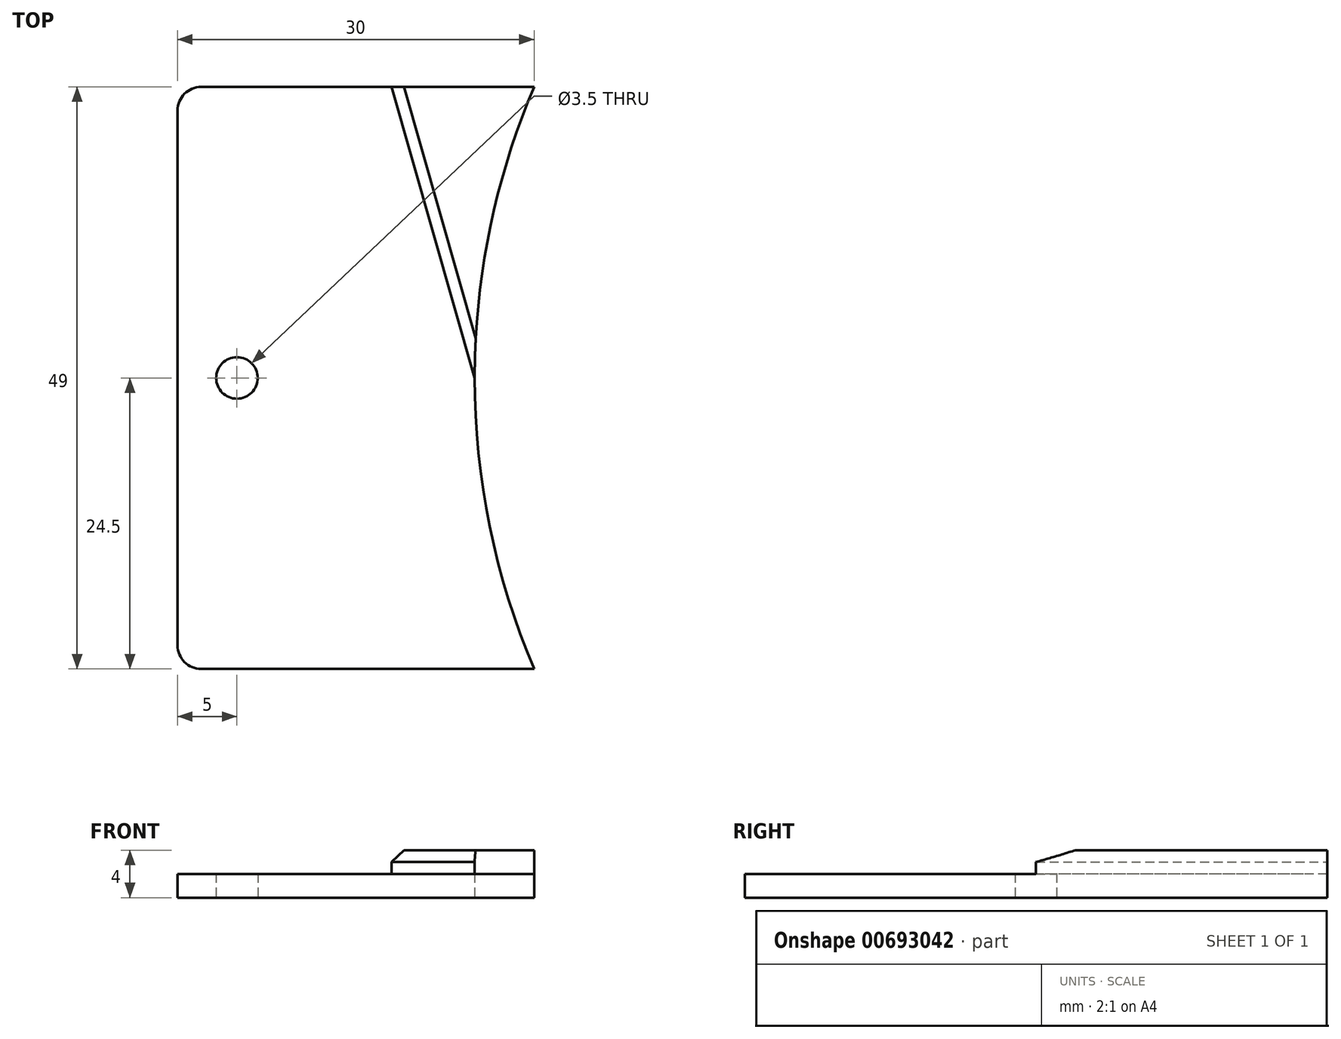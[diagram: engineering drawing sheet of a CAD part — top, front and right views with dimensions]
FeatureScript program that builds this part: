
annotation { "Feature Type Name" : "Feature", "Feature Type Description" : "" }
export const myFeature = defineFeature(function(context is Context, id is Id, definition is map)
    precondition{}
    {
        {
            var Q0;
            Q0=qCreatedBy(makeId("Top.planeOp"),FACE);
            var sketch = newSketch(context, id + "F0", { "sketchPlane" : qUnion([Q0])});
            skLineSegment(sketch, "E0", {"start": v(0, 0) * mm, "end": v(-100, 0) * mm, "construction": true});
            skLineSegment(sketch, "E1.bottom", {"start": v(-87.5, 24.5) * mm, "end": v(-27.5, 24.5) * mm});
            skLineSegment(sketch, "E1.top", {"start": v(-87.5, -24.5) * mm, "end": v(-27.5, -24.5) * mm});
            skLineSegment(sketch, "E1.left", {"start": v(-87.5, 24.5) * mm, "end": v(-87.5, -24.5) * mm});
            skLineSegment(sketch, "E1.right", {"start": v(-27.5, 24.5) * mm, "end": v(-27.5, -24.5) * mm});
            skPoint(sketch, "E1.middle", {"position": v(-57.5, 0) * mm});
            skCircle(sketch, "E2", {"center": v(0, 0) * mm, "radius": 62.5 * mm});
            skPoint(sketch, "E3", {"position": v(-69.5, 24.5) * mm});
            skPoint(sketch, "E4", {"position": v(-62.5, 0) * mm});
            skLineSegment(sketch, "E5", {"start": v(-69.5, 24.5) * mm, "end": v(-62.5, 0) * mm});
            skCircle(sketch, "E6", {"center": v(-82.5, 0) * mm, "radius": 1.75 * mm});
            skSolve(sketch);
        }
        {
            var Q0;
            {var subQ0=sQuery(id+"F0.wireOp",EDGE,"E5");Q0=makeQuery(id+"F0.imprint","IMPRINT",FACE,{"disambiguationData":[TD([[makeQuery(id+"F0.imprint","IMPRINT",EDGE,{"derivedFrom":subQ0}),1.0]])]});}
            extrude(context, id + "F1", {"entities" : qUnion([Q0]), "depth" : 4 * mm, "offsetDistance" : 25 * mm});
        }
        {
            var Q0;
            {var subQ4=sQuery(id+"F0.wireOp",EDGE,"E1.left");Q0=makeQuery(id+"F0.imprint","IMPRINT",FACE,{"disambiguationData":[TD([[makeQuery(id+"F0.imprint","IMPRINT",EDGE,{"derivedFrom":subQ4}),1.0]])]});}
            extrude(context, id + "F2", {"entities" : qUnion([Q0]), "operationType" : NewBodyOperationType.ADD, "depth" : 2 * mm, "offsetDistance" : 25 * mm});
        }
        {
            var Q0;
            Q0=makeQuery(id+"F1.opExtrude","CAP_EDGE",EDGE,{"disambiguationData":[OSD([sQuery(id+"F0.wireOp",EDGE,"E5")])],"isStart":false});
            chamfer(context, id + "F3", {"entities" : qUnion([Q0]), "width" : 1 * mm, "tangentPropagation" : true});
        }
        {
            var Q0;
            Q0=makeQuery(id+"F2.opExtrude","SWEPT_EDGE",EDGE,{"disambiguationData":[OSD([sQuery(id+"F0.wireOp",EDGE,"E1.top"),sQuery(id+"F0.wireOp",EDGE,"E1.left")])]});
            var Q1;
            Q1=makeQuery(id+"F2.opExtrude","SWEPT_EDGE",EDGE,{"disambiguationData":[OSD([sQuery(id+"F0.wireOp",EDGE,"E1.bottom"),sQuery(id+"F0.wireOp",EDGE,"E1.left")])]});
            fillet(context, id + "F4", {"entities" : qUnion([Q0, Q1]), "radius" : 2 * mm, "tangentPropagation" : true, "allowEdgeOverflow" : false});
        }
    });
